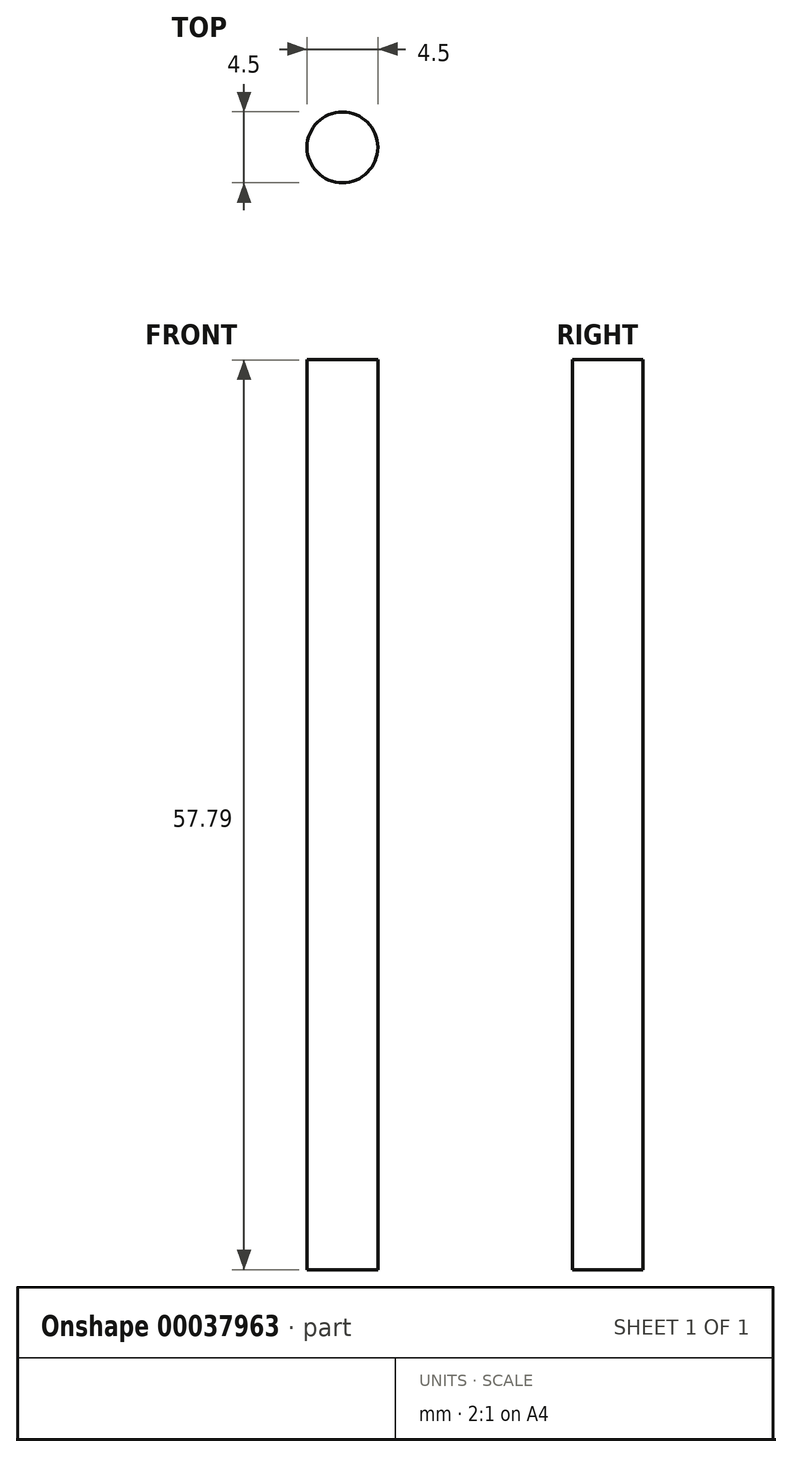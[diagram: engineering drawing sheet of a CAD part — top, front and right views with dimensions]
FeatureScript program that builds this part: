
annotation { "Feature Type Name" : "Feature", "Feature Type Description" : "" }
export const myFeature = defineFeature(function(context is Context, id is Id, definition is map)
    precondition{}
    {
        {
            var Q0;
            Q0=qCreatedBy(makeId("Top.planeOp"),FACE);
            var sketch = newSketch(context, id + "F0", { "sketchPlane" : qUnion([Q0])});
            skCircle(sketch, "E0", {"center": v(0, 0) * mm, "radius": 2.25 * mm});
            skSolve(sketch);
        }
        {
            var Q0;
            Q0 = qSketchRegion(id + "F0", true);
            extrude(context, id + "F1", {"entities" : qUnion([Q0]), "depth" : 57.8 * mm});
        }
    });
